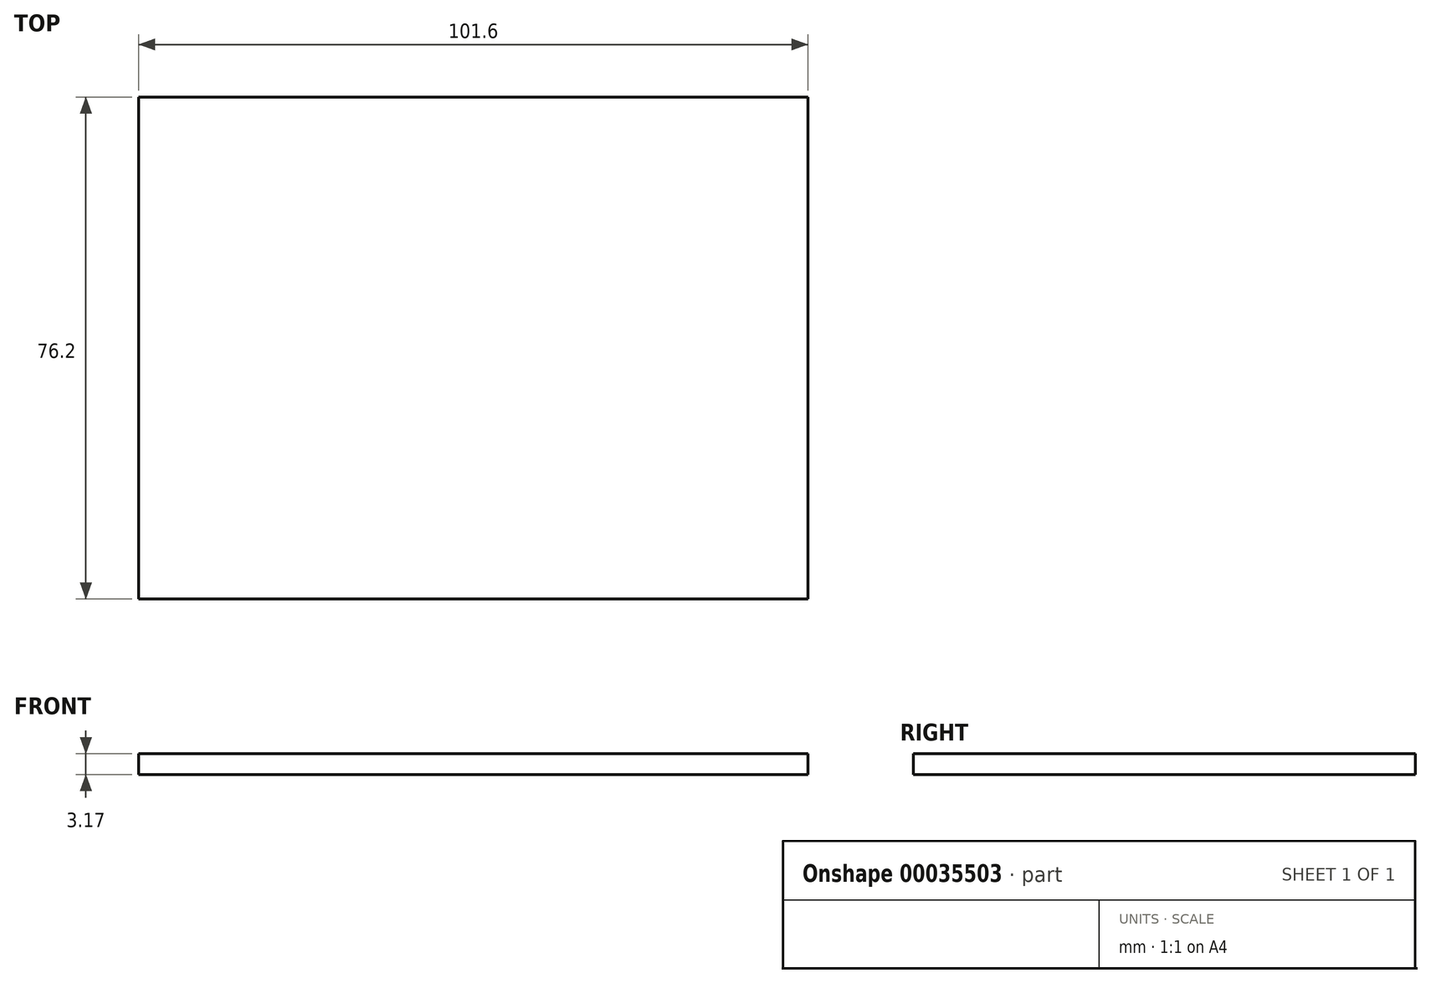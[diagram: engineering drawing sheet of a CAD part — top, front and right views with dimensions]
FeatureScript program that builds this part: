
annotation { "Feature Type Name" : "Feature", "Feature Type Description" : "" }
export const myFeature = defineFeature(function(context is Context, id is Id, definition is map)
    precondition{}
    {
        {
            var Q0;
            Q0=qCreatedBy(makeId("Top.planeOp"),FACE);
            var sketch = newSketch(context, id + "F0", { "sketchPlane" : qUnion([Q0])});
            skLineSegment(sketch, "E0.rect.bottom", {"start": v(50.8, 38.1) * mm, "end": v(-50.8, 38.1) * mm});
            skLineSegment(sketch, "E0.rect.top", {"start": v(50.8, -38.1) * mm, "end": v(-50.8, -38.1) * mm});
            skLineSegment(sketch, "E0.rect.left", {"start": v(50.8, 38.1) * mm, "end": v(50.8, -38.1) * mm});
            skLineSegment(sketch, "E0.rect.right", {"start": v(-50.8, 38.1) * mm, "end": v(-50.8, -38.1) * mm});
            skPoint(sketch, "E0.rect.middle", {"position": v(0, 0) * mm});
            skSolve(sketch);
        }
        {
            var Q0;
            Q0=makeQuery(id+"F0.imprint","IMPRINT",FACE,{"disambiguationData":[TD([[makeQuery(id+"F0.imprint","IMPRINT",EDGE,{"derivedFrom":sQuery(id+"F0.wireOp",EDGE,"E0.rect.bottom")}),1.0]])]});
            extrude(context, id + "F1", {"entities" : qUnion([Q0]), "depth" : 3.17 * mm});
        }
    });
